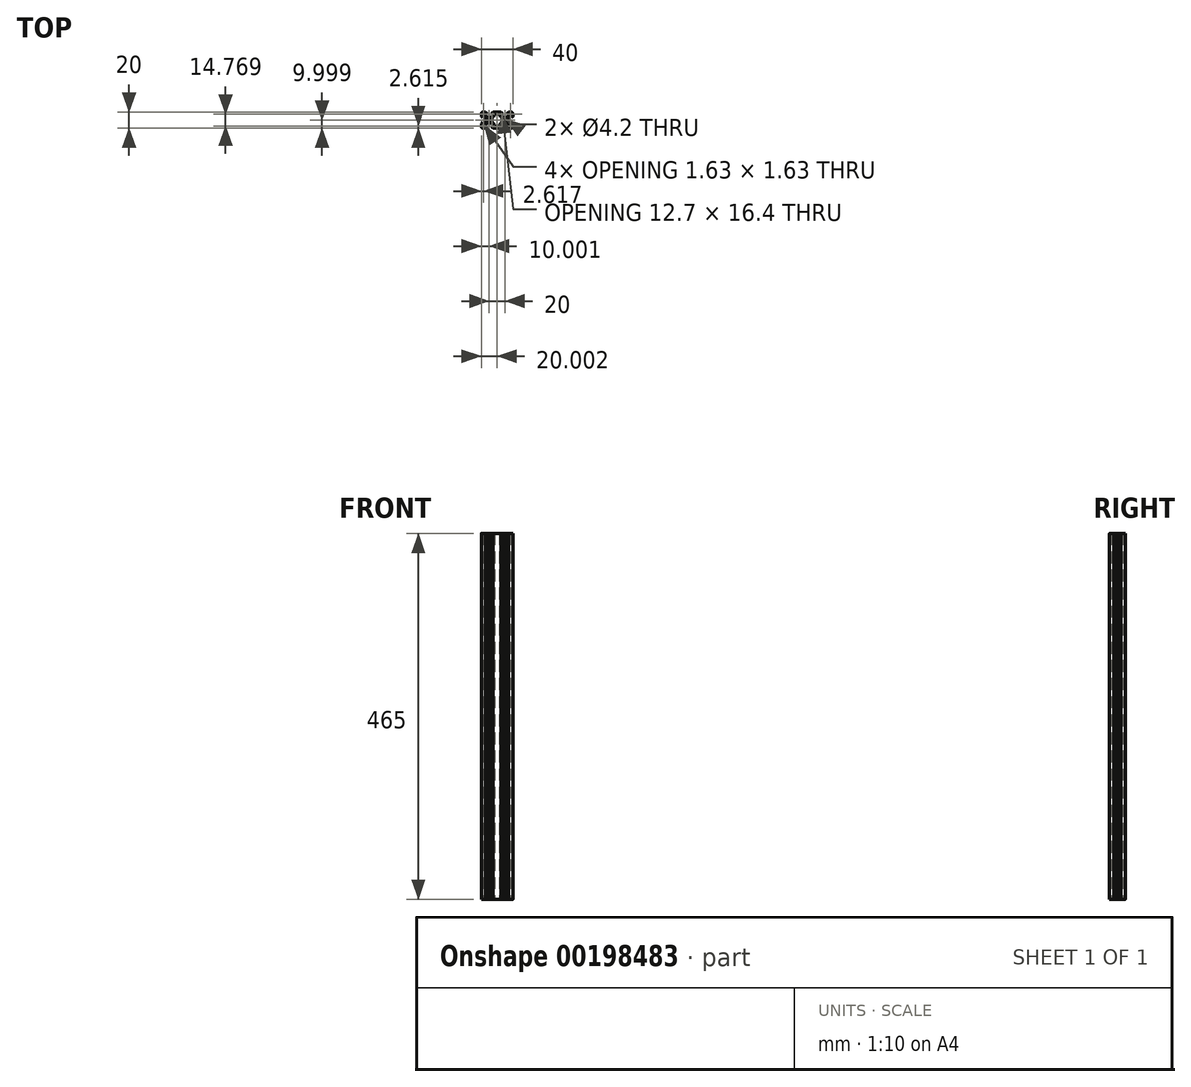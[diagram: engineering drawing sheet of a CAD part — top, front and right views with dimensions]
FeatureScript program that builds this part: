
annotation { "Feature Type Name" : "Feature", "Feature Type Description" : "" }
export const myFeature = defineFeature(function(context is Context, id is Id, definition is map)
    precondition{}
    {
        {
            var Q0;
            Q0=qCreatedBy(makeId("Top.planeOp"),FACE);
            var sketch = newSketch(context, id + "F0", { "sketchPlane" : qUnion([Q0])});
            skLineSegment(sketch, "E0", {"start": v(-1.54, -10.06) * mm, "end": v(-5.4, -10.06) * mm});
            skLineSegment(sketch, "E1", {"start": v(-20.04, -8.56) * mm, "end": v(-20.04, -4.7) * mm});
            skLineSegment(sketch, "E2", {"start": v(-18.54, 9.94) * mm, "end": v(-14.68, 9.94) * mm});
            skLineSegment(sketch, "E3.0", {"start": v(-15.54, 8.14) * mm, "end": v(-12.88, 8.14) * mm});
            skLineSegment(sketch, "E3.1", {"start": v(-18.24, -5.56) * mm, "end": v(-18.24, -2.9) * mm});
            skLineSegment(sketch, "E3.2", {"start": v(-4.54, -8.26) * mm, "end": v(-7.2, -8.26) * mm});
            skLineSegment(sketch, "E4.trimOffspring", {"start": v(-5.4, 9.94) * mm, "end": v(-1.54, 9.94) * mm});
            skLineSegment(sketch, "E5", {"start": v(-12.88, 8.14) * mm, "end": v(-14.68, 9.94) * mm});
            skLineSegment(sketch, "E6.trimOffspring", {"start": v(-7.2, 8.14) * mm, "end": v(-4.54, 8.14) * mm});
            skLineSegment(sketch, "E7.MirrorCS", {"start": v(-7.2, 8.14) * mm, "end": v(-5.4, 9.94) * mm});
            skLineSegment(sketch, "E8.MirrorCS", {"start": v(-7.2, -8.26) * mm, "end": v(-5.4, -10.06) * mm});
            skLineSegment(sketch, "E9.MirrorCS", {"start": v(-12.88, -8.26) * mm, "end": v(-14.68, -10.06) * mm});
            skLineSegment(sketch, "E10.trimOffspring", {"start": v(-12.88, -8.26) * mm, "end": v(-15.54, -8.26) * mm});
            skLineSegment(sketch, "E11.trimOffspring", {"start": v(-14.68, -10.06) * mm, "end": v(-18.54, -10.06) * mm});
            skLineSegment(sketch, "E12", {"start": v(-18.24, 2.78) * mm, "end": v(-20.04, 4.58) * mm});
            skLineSegment(sketch, "E13", {"start": v(-18.24, -2.9) * mm, "end": v(-20.04, -4.7) * mm});
            skLineSegment(sketch, "E14.trimOffspring", {"start": v(-20.04, 4.58) * mm, "end": v(-20.04, 8.44) * mm});
            skLineSegment(sketch, "E15.trimOffspring", {"start": v(-18.24, 2.78) * mm, "end": v(-18.24, 5.44) * mm});
            skCircle(sketch, "E16", {"center": v(-10.04, -0.06) * mm, "radius": 2.1 * mm});
            skLineSegment(sketch, "E17", {"start": v(-16.6, 5.44) * mm, "end": v(-13.94, 2.78) * mm});
            skLineSegment(sketch, "E18", {"start": v(-15.54, 6.5) * mm, "end": v(-12.88, 3.84) * mm});
            skLineSegment(sketch, "E19", {"start": v(-15.54, 6.5) * mm, "end": v(-15.54, 8.14) * mm});
            skLineSegment(sketch, "E20", {"start": v(-16.6, 5.44) * mm, "end": v(-18.24, 5.44) * mm});
            skLineSegment(sketch, "E21", {"start": v(-3.48, 5.44) * mm, "end": v(-6.14, 2.78) * mm});
            skLineSegment(sketch, "E22", {"start": v(-4.54, 6.5) * mm, "end": v(-7.2, 3.84) * mm});
            skLineSegment(sketch, "E23", {"start": v(-16.6, -5.56) * mm, "end": v(-18.24, -5.56) * mm});
            skLineSegment(sketch, "E24", {"start": v(-15.54, -6.62) * mm, "end": v(-15.54, -8.26) * mm});
            skLineSegment(sketch, "E25", {"start": v(-4.54, 6.5) * mm, "end": v(-4.54, 8.14) * mm});
            skLineSegment(sketch, "E26", {"start": v(-4.54, -6.62) * mm, "end": v(-4.54, -8.26) * mm});
            skLineSegment(sketch, "E27.trimOffspring", {"start": v(-7.2, -3.96) * mm, "end": v(-4.54, -6.62) * mm});
            skLineSegment(sketch, "E28.trimOffspring", {"start": v(-12.88, -3.96) * mm, "end": v(-15.54, -6.62) * mm});
            skLineSegment(sketch, "E29.trimOffspring", {"start": v(-13.94, -2.9) * mm, "end": v(-16.6, -5.56) * mm});
            skLineSegment(sketch, "E30.trimOffspring", {"start": v(-6.14, -2.9) * mm, "end": v(-3.48, -5.56) * mm});
            skLineSegment(sketch, "E31", {"start": v(-13.94, -2.9) * mm, "end": v(-13.94, -0.31) * mm});
            skLineSegment(sketch, "E32", {"start": v(-12.88, 3.84) * mm, "end": v(-10.29, 3.84) * mm});
            skLineSegment(sketch, "E33", {"start": v(-12.88, -3.96) * mm, "end": v(-10.29, -3.96) * mm});
            skLineSegment(sketch, "E34", {"start": v(-6.14, 2.78) * mm, "end": v(-6.14, 0.19) * mm});
            skLineSegment(sketch, "E35", {"start": v(-18.24, 6.5) * mm, "end": v(-18.24, 8.14) * mm});
            skLineSegment(sketch, "E36", {"start": v(-16.6, 8.14) * mm, "end": v(-18.24, 8.14) * mm});
            skLineSegment(sketch, "E37", {"start": v(-18.24, 6.5) * mm, "end": v(-17.67, 6.5) * mm});
            skLineSegment(sketch, "E38", {"start": v(-16.6, 8.14) * mm, "end": v(-16.6, 7.57) * mm});
            skLineSegment(sketch, "E39", {"start": v(-17.67, 6.5) * mm, "end": v(-16.6, 7.57) * mm});
            skLineSegment(sketch, "E40.MirrorCS", {"start": v(-16.6, -8.26) * mm, "end": v(-18.24, -8.26) * mm});
            skLineSegment(sketch, "E41.MirrorCS", {"start": v(-18.24, -6.63) * mm, "end": v(-17.67, -6.63) * mm});
            skLineSegment(sketch, "E42.MirrorCS", {"start": v(-18.24, -6.63) * mm, "end": v(-18.24, -8.26) * mm});
            skLineSegment(sketch, "E43.MirrorCS", {"start": v(-17.67, -6.63) * mm, "end": v(-16.6, -7.7) * mm});
            skLineSegment(sketch, "E44.MirrorCS", {"start": v(-16.6, -8.26) * mm, "end": v(-16.6, -7.7) * mm});
            skArc(sketch, "E45.filletArc", {"start": v(-18.54, 9.94) * mm, "mid": v(-19.6, 9.5) * mm, "end": v(-20.04, 8.44) * mm});
            skPoint(sketch, "E46.visualSharp", {"position": v(-0.04, 9.94) * mm});
            skArc(sketch, "E47.filletArc", {"start": v(-20.04, -8.56) * mm, "mid": v(-19.6, -9.62) * mm, "end": v(-18.54, -10.06) * mm});
            skLineSegment(sketch, "E48", {"start": v(-13.69, -0.06) * mm, "end": v(-13.94, 0.19) * mm});
            skLineSegment(sketch, "E49.MirrorCS", {"start": v(-13.69, -0.06) * mm, "end": v(-13.94, -0.31) * mm});
            skLineSegment(sketch, "E50.trimOffspring", {"start": v(-13.94, 0.19) * mm, "end": v(-13.94, 2.78) * mm});
            skLineSegment(sketch, "E51.MirrorCS", {"start": v(-6.39, -0.06) * mm, "end": v(-6.14, 0.19) * mm});
            skLineSegment(sketch, "E52.MirrorCS", {"start": v(-6.39, -0.06) * mm, "end": v(-6.14, -0.31) * mm});
            skLineSegment(sketch, "E53", {"start": v(-10.04, -3.71) * mm, "end": v(-9.79, -3.96) * mm});
            skLineSegment(sketch, "E54.MirrorCS", {"start": v(-10.04, -3.71) * mm, "end": v(-10.29, -3.96) * mm});
            skLineSegment(sketch, "E55.trimOffspring", {"start": v(-9.79, -3.96) * mm, "end": v(-7.2, -3.96) * mm});
            skLineSegment(sketch, "E56.trimOffspring", {"start": v(-6.14, -0.31) * mm, "end": v(-6.14, -2.9) * mm});
            skLineSegment(sketch, "E57.MirrorCS", {"start": v(-10.04, 3.59) * mm, "end": v(-10.29, 3.84) * mm});
            skLineSegment(sketch, "E58.MirrorCS", {"start": v(-10.04, 3.59) * mm, "end": v(-9.79, 3.84) * mm});
            skLineSegment(sketch, "E59.trimOffspring", {"start": v(-9.79, 3.84) * mm, "end": v(-7.2, 3.84) * mm});
            skLineSegment(sketch, "E60.MirrorCS", {"start": v(9.96, -3.71) * mm, "end": v(9.71, -3.96) * mm});
            skLineSegment(sketch, "E61.MirrorCS", {"start": v(9.96, -3.71) * mm, "end": v(10.21, -3.96) * mm});
            skLineSegment(sketch, "E62.MirrorCS", {"start": v(13.61, -0.06) * mm, "end": v(13.86, 0.19) * mm});
            skLineSegment(sketch, "E63.MirrorCS", {"start": v(13.61, -0.06) * mm, "end": v(13.86, -0.31) * mm});
            skLineSegment(sketch, "E64.MirrorCS", {"start": v(6.31, -0.06) * mm, "end": v(6.06, 0.19) * mm});
            skLineSegment(sketch, "E65.MirrorCS", {"start": v(6.31, -0.06) * mm, "end": v(6.06, -0.31) * mm});
            skLineSegment(sketch, "E66.MirrorCS", {"start": v(18.16, -6.63) * mm, "end": v(17.6, -6.63) * mm});
            skLineSegment(sketch, "E67.MirrorCS", {"start": v(9.96, 3.59) * mm, "end": v(10.21, 3.84) * mm});
            skLineSegment(sketch, "E68.MirrorCS", {"start": v(9.96, 3.59) * mm, "end": v(9.71, 3.84) * mm});
            skLineSegment(sketch, "E69.MirrorCS", {"start": v(18.16, 6.5) * mm, "end": v(17.6, 6.5) * mm});
            skLineSegment(sketch, "E70.MirrorCS", {"start": v(16.53, -8.26) * mm, "end": v(16.53, -7.7) * mm});
            skLineSegment(sketch, "E71.MirrorCS", {"start": v(16.53, 8.14) * mm, "end": v(16.53, 7.57) * mm});
            skLineSegment(sketch, "E72.MirrorCS", {"start": v(18.16, 2.78) * mm, "end": v(18.16, 5.44) * mm});
            skLineSegment(sketch, "E73.MirrorCS", {"start": v(4.46, -6.62) * mm, "end": v(4.46, -8.26) * mm});
            skArc(sketch, "E74.MirrorCS", {"start": v(19.96, -8.56) * mm, "mid": v(19.52, -9.62) * mm, "end": v(18.46, -10.06) * mm});
            skLineSegment(sketch, "E75.MirrorCS", {"start": v(7.12, -3.96) * mm, "end": v(4.46, -6.62) * mm});
            skLineSegment(sketch, "E76.MirrorCS", {"start": v(12.8, -3.96) * mm, "end": v(15.46, -6.62) * mm});
            skPoint(sketch, "E77.MirrorP", {"position": v(-0.04, -10.06) * mm});
            skLineSegment(sketch, "E78.MirrorCS", {"start": v(13.86, -2.9) * mm, "end": v(16.52, -5.56) * mm});
            skLineSegment(sketch, "E79.MirrorCS", {"start": v(13.86, 0.19) * mm, "end": v(13.86, 2.78) * mm});
            skLineSegment(sketch, "E80.MirrorCS", {"start": v(6.06, -2.9) * mm, "end": v(3.4, -5.56) * mm});
            skCircle(sketch, "E81.MirrorC", {"center": v(9.96, -0.06) * mm, "radius": 2.1 * mm});
            skLineSegment(sketch, "E82.MirrorCS", {"start": v(13.86, -2.9) * mm, "end": v(13.86, -0.31) * mm});
            skLineSegment(sketch, "E83.MirrorCS", {"start": v(16.52, 5.44) * mm, "end": v(13.86, 2.78) * mm});
            skLineSegment(sketch, "E84.MirrorCS", {"start": v(12.8, 3.84) * mm, "end": v(10.21, 3.84) * mm});
            skLineSegment(sketch, "E85.MirrorCS", {"start": v(15.46, 6.5) * mm, "end": v(12.8, 3.84) * mm});
            skLineSegment(sketch, "E86.MirrorCS", {"start": v(12.8, -3.96) * mm, "end": v(10.21, -3.96) * mm});
            skLineSegment(sketch, "E87.MirrorCS", {"start": v(15.46, 6.5) * mm, "end": v(15.46, 8.14) * mm});
            skLineSegment(sketch, "E88.MirrorCS", {"start": v(6.06, -0.31) * mm, "end": v(6.06, -2.9) * mm});
            skLineSegment(sketch, "E89.MirrorCS", {"start": v(18.16, 6.5) * mm, "end": v(18.16, 8.14) * mm});
            skLineSegment(sketch, "E90.MirrorCS", {"start": v(3.4, 5.44) * mm, "end": v(6.06, 2.78) * mm});
            skLineSegment(sketch, "E91.MirrorCS", {"start": v(16.53, -8.26) * mm, "end": v(18.16, -8.26) * mm});
            skLineSegment(sketch, "E92.MirrorCS", {"start": v(6.06, 2.78) * mm, "end": v(6.06, 0.19) * mm});
            skLineSegment(sketch, "E93.MirrorCS", {"start": v(16.52, 5.44) * mm, "end": v(18.16, 5.44) * mm});
            skLineSegment(sketch, "E94.MirrorCS", {"start": v(9.71, -3.96) * mm, "end": v(7.12, -3.96) * mm});
            skLineSegment(sketch, "E95.MirrorCS", {"start": v(18.16, -6.63) * mm, "end": v(18.16, -8.26) * mm});
            skLineSegment(sketch, "E96.MirrorCS", {"start": v(16.53, 8.14) * mm, "end": v(18.16, 8.14) * mm});
            skLineSegment(sketch, "E97.MirrorCS", {"start": v(4.46, 6.5) * mm, "end": v(7.12, 3.84) * mm});
            skLineSegment(sketch, "E98.MirrorCS", {"start": v(17.6, -6.63) * mm, "end": v(16.53, -7.7) * mm});
            skLineSegment(sketch, "E99.MirrorCS", {"start": v(16.52, -5.56) * mm, "end": v(18.16, -5.56) * mm});
            skLineSegment(sketch, "E100.MirrorCS", {"start": v(12.8, -8.26) * mm, "end": v(14.6, -10.06) * mm});
            skLineSegment(sketch, "E101.MirrorCS", {"start": v(12.8, -8.26) * mm, "end": v(15.46, -8.26) * mm});
            skLineSegment(sketch, "E102.MirrorCS", {"start": v(14.6, -10.06) * mm, "end": v(18.46, -10.06) * mm});
            skLineSegment(sketch, "E103.MirrorCS", {"start": v(1.46, -10.06) * mm, "end": v(5.32, -10.06) * mm});
            skLineSegment(sketch, "E104.MirrorCS", {"start": v(19.96, -8.56) * mm, "end": v(19.96, -4.7) * mm});
            skLineSegment(sketch, "E105.MirrorCS", {"start": v(18.46, 9.94) * mm, "end": v(14.6, 9.94) * mm});
            skLineSegment(sketch, "E106.MirrorCS", {"start": v(15.46, 8.14) * mm, "end": v(12.8, 8.14) * mm});
            skLineSegment(sketch, "E107.MirrorCS", {"start": v(18.16, -5.56) * mm, "end": v(18.16, -2.9) * mm});
            skLineSegment(sketch, "E108.MirrorCS", {"start": v(4.46, -8.26) * mm, "end": v(7.12, -8.26) * mm});
            skLineSegment(sketch, "E109.MirrorCS", {"start": v(5.32, 9.94) * mm, "end": v(1.46, 9.94) * mm});
            skLineSegment(sketch, "E110.MirrorCS", {"start": v(12.8, 8.14) * mm, "end": v(14.6, 9.94) * mm});
            skLineSegment(sketch, "E111.MirrorCS", {"start": v(7.12, 8.14) * mm, "end": v(4.46, 8.14) * mm});
            skLineSegment(sketch, "E112.MirrorCS", {"start": v(7.12, 8.14) * mm, "end": v(5.32, 9.94) * mm});
            skLineSegment(sketch, "E113.MirrorCS", {"start": v(7.12, -8.26) * mm, "end": v(5.32, -10.06) * mm});
            skLineSegment(sketch, "E114.MirrorCS", {"start": v(18.16, 2.78) * mm, "end": v(19.96, 4.58) * mm});
            skLineSegment(sketch, "E115.MirrorCS", {"start": v(9.71, 3.84) * mm, "end": v(7.12, 3.84) * mm});
            skLineSegment(sketch, "E116.MirrorCS", {"start": v(15.46, -6.62) * mm, "end": v(15.46, -8.26) * mm});
            skLineSegment(sketch, "E117.MirrorCS", {"start": v(18.16, -2.9) * mm, "end": v(19.96, -4.7) * mm});
            skArc(sketch, "E118.MirrorCS", {"start": v(18.46, 9.94) * mm, "mid": v(19.52, 9.5) * mm, "end": v(19.96, 8.44) * mm});
            skLineSegment(sketch, "E119.MirrorCS", {"start": v(17.6, 6.5) * mm, "end": v(16.53, 7.57) * mm});
            skLineSegment(sketch, "E120.MirrorCS", {"start": v(4.46, 6.5) * mm, "end": v(4.46, 8.14) * mm});
            skLineSegment(sketch, "E121.MirrorCS", {"start": v(19.96, 4.58) * mm, "end": v(19.96, 8.44) * mm});
            skLineSegment(sketch, "E122", {"start": v(-1.54, 9.94) * mm, "end": v(1.46, 9.94) * mm});
            skLineSegment(sketch, "E123", {"start": v(-1.54, -10.06) * mm, "end": v(1.46, -10.06) * mm});
            skLineSegment(sketch, "E124", {"start": v(-3.04, 8.14) * mm, "end": v(2.96, 8.14) * mm});
            skLineSegment(sketch, "E125", {"start": v(-3.04, -8.26) * mm, "end": v(-3.04, -6) * mm});
            skLineSegment(sketch, "E126", {"start": v(-6.14, -2.9) * mm, "end": v(-3.04, -6) * mm});
            skLineSegment(sketch, "E127", {"start": v(2.96, -8.26) * mm, "end": v(2.96, -6) * mm});
            skLineSegment(sketch, "E128", {"start": v(6.06, -2.9) * mm, "end": v(2.96, -6) * mm});
            skLineSegment(sketch, "E129", {"start": v(-3.04, -8.26) * mm, "end": v(2.96, -8.26) * mm});
            skLineSegment(sketch, "E130", {"start": v(6.06, 2.78) * mm, "end": v(2.96, 5.88) * mm});
            skLineSegment(sketch, "E131", {"start": v(-6.14, 2.78) * mm, "end": v(-3.48, 5.44) * mm});
            skLineSegment(sketch, "E132", {"start": v(-3.48, 5.44) * mm, "end": v(-3.04, 5.88) * mm});
            skLineSegment(sketch, "E133.trimOffspring", {"start": v(-3.04, 5.88) * mm, "end": v(-3.04, 8.14) * mm});
            skLineSegment(sketch, "E134", {"start": v(2.96, 5.88) * mm, "end": v(2.96, 8.14) * mm});
            skSolve(sketch);
        }
        {
            var Q0;
            Q0 = qSketchRegion(id + "F0", true);
            extrude(context, id + "F1", {"entities" : qUnion([Q0]), "depth" : 465 * mm});
        }
    });
